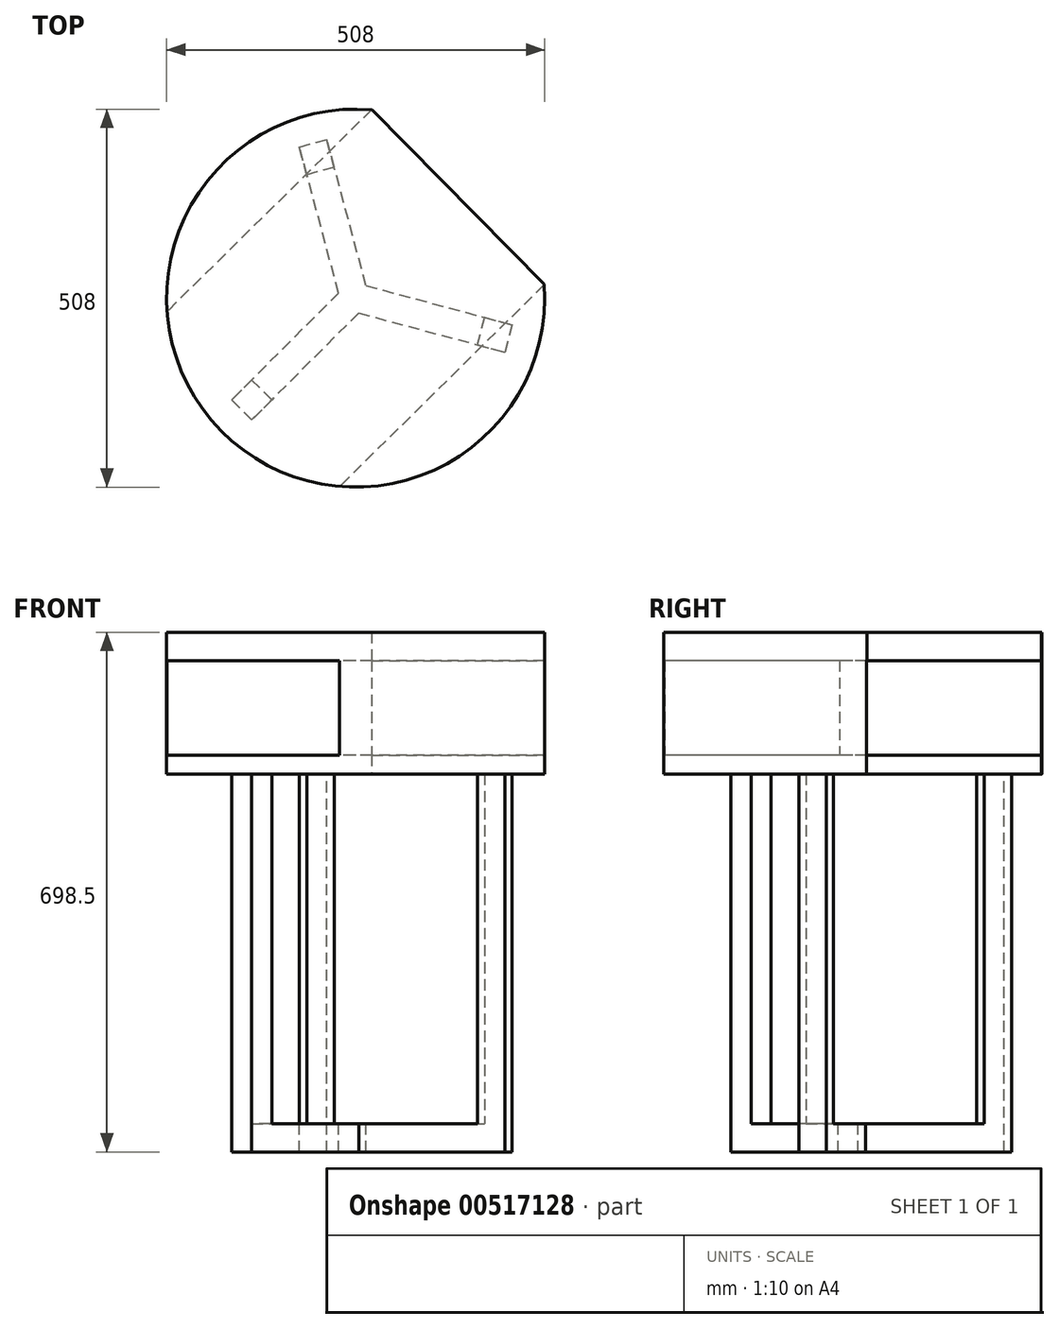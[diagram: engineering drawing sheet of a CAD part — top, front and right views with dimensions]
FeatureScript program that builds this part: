
annotation { "Feature Type Name" : "Feature", "Feature Type Description" : "" }
export const myFeature = defineFeature(function(context is Context, id is Id, definition is map)
    precondition{}
    {
        {
            var Q0;
            Q0=qCreatedBy(makeId("Top.planeOp"),FACE);
            var sketch = newSketch(context, id + "F0", { "sketchPlane" : qUnion([Q0])});
            skLineSegment(sketch, "E0", {"start": v(-200.85, -173.93) * mm, "end": v(-173.93, -200.85) * mm});
            skLineSegment(sketch, "E1", {"start": v(-173.93, -200.85) * mm, "end": v(-164.05, -164.05) * mm});
            skLineSegment(sketch, "E2", {"start": v(-200.85, -173.93) * mm, "end": v(-344.53, -317.6) * mm});
            skLineSegment(sketch, "E3", {"start": v(-173.93, -200.85) * mm, "end": v(-317.63, -344.55) * mm});
            skLineSegment(sketch, "E4", {"start": v(-317.63, -344.55) * mm, "end": v(-344.53, -317.6) * mm});
            skLineSegment(sketch, "E5", {"start": v(-173.93, -200.85) * mm, "end": v(22.33, -253.51) * mm});
            skLineSegment(sketch, "E6", {"start": v(-164.05, -164.05) * mm, "end": v(32.2, -216.71) * mm});
            skLineSegment(sketch, "E7", {"start": v(32.2, -216.71) * mm, "end": v(22.33, -253.51) * mm});
            skLineSegment(sketch, "E8", {"start": v(-200.85, -173.93) * mm, "end": v(-164.05, -164.05) * mm});
            skLineSegment(sketch, "E9", {"start": v(-164.05, -164.05) * mm, "end": v(-216.71, 32.2) * mm});
            skLineSegment(sketch, "E10", {"start": v(-200.85, -173.93) * mm, "end": v(-253.51, 22.33) * mm});
            skLineSegment(sketch, "E11", {"start": v(-253.51, 22.33) * mm, "end": v(-216.71, 32.2) * mm});
            skLineSegment(sketch, "E12", {"start": v(-317.6, -290.67) * mm, "end": v(-290.69, -317.6) * mm});
            skLineSegment(sketch, "E13", {"start": v(-14.47, -243.64) * mm, "end": v(-4.6, -206.84) * mm});
            skLineSegment(sketch, "E14", {"start": v(-243.64, -14.47) * mm, "end": v(-206.84, -4.6) * mm});
            skSolve(sketch);
        }
        {
            var Q0;
            Q0 = qSketchRegion(id + "F0", true);
            extrude(context, id + "F1", {"entities" : qUnion([Q0]), "oppositeDirection" : true, "depth" : 38.1 * mm, "offsetDistance" : 25.4 * mm});
        }
        {
            var Q0;
            {var subQ0=sQuery(id+"F0.wireOp",EDGE,"E4");Q0=makeQuery(id+"F0.imprint","IMPRINT",FACE,{"disambiguationData":[TD([[makeQuery(id+"F0.imprint","IMPRINT",EDGE,{"derivedFrom":subQ0}),-1.0]])]});}
            extrude(context, id + "F2", {"entities" : qUnion([Q0]), "operationType" : NewBodyOperationType.ADD, "depth" : 469.9 * mm, "offsetDistance" : 25.4 * mm});
        }
        {
            var Q0;
            {var subQ0=sQuery(id+"F0.wireOp",EDGE,"E7");Q0=makeQuery(id+"F0.imprint","IMPRINT",FACE,{"disambiguationData":[TD([[makeQuery(id+"F0.imprint","IMPRINT",EDGE,{"derivedFrom":subQ0}),-1.0]])]});}
            extrude(context, id + "F3", {"entities" : qUnion([Q0]), "operationType" : NewBodyOperationType.ADD, "depth" : 469.9 * mm, "offsetDistance" : 25.4 * mm});
        }
        {
            var Q0;
            {var subQ0=sQuery(id+"F0.wireOp",EDGE,"E11");Q0=makeQuery(id+"F0.imprint","IMPRINT",FACE,{"disambiguationData":[TD([[makeQuery(id+"F0.imprint","IMPRINT",EDGE,{"derivedFrom":subQ0}),-1.0]])]});}
            extrude(context, id + "F4", {"entities" : qUnion([Q0]), "operationType" : NewBodyOperationType.ADD, "depth" : 469.9 * mm, "offsetDistance" : 25.4 * mm});
        }
        {
            var Q0;
            Q0=makeQuery(id+"F2.opExtrude","CAP_FACE",FACE,{"disambiguationData":[OSD([sQuery(id+"F0.wireOp",EDGE,"E2"),sQuery(id+"F0.wireOp",EDGE,"E3"),sQuery(id+"F0.wireOp",EDGE,"E4"),sQuery(id+"F0.wireOp",EDGE,"E12")])],"isStart":false});
            var sketch = newSketch(context, id + "F5", { "sketchPlane" : qUnion([Q0])});
            skArc(sketch, "E15", {"start": v(-156.5, 72.26) * mm, "mid": v(-358.81, -359.2) * mm, "end": v(75.38, -162.82) * mm});
            skLineSegment(sketch, "E16", {"start": v(-156.5, 72.26) * mm, "end": v(75.38, -162.82) * mm});
            skPoint(sketch, "E17.end.orphan", {"position": v(-356.35, 0) * mm});
            skSolve(sketch);
        }
        {
            var Q0;
            Q0 = qSketchRegion(id + "F5", true);
            extrude(context, id + "F6", {"entities" : qUnion([Q0]), "operationType" : NewBodyOperationType.ADD, "depth" : 25.4 * mm, "offsetDistance" : 25.4 * mm});
        }
        {
            var Q0;
            Q0=makeQuery(id+"F6.opExtrude","CAP_FACE",FACE,{"disambiguationData":[OSD([sQuery(id+"F5.wireOp",EDGE,"E15")])],"isStart":false});
            var sketch = newSketch(context, id + "F7", { "sketchPlane" : qUnion([Q0])});
            skArc(sketch, "E18", {"start": v(-199.46, -433.92) * mm, "mid": v(0.39, -361.66) * mm, "end": v(75.38, -162.82) * mm});
            skLineSegment(sketch, "E19", {"start": v(75.38, -162.82) * mm, "end": v(137.4, -101.64) * mm});
            skLineSegment(sketch, "E20", {"start": v(75.38, -162.82) * mm, "end": v(-199.46, -433.92) * mm});
            skLineSegment(sketch, "E21", {"start": v(-156.5, 72.26) * mm, "end": v(-431.34, -198.84) * mm});
            skPoint(sketch, "E22.orphan", {"position": v(0.39, -361.66) * mm});
            skPoint(sketch, "E23.end.orphan", {"position": v(-356.35, 0) * mm});
            skArc(sketch, "E24.trimOffspring", {"start": v(-156.5, 72.26) * mm, "mid": v(-356.35, 0) * mm, "end": v(-431.34, -198.84) * mm});
            skLineSegment(sketch, "E25", {"start": v(-199.46, -433.92) * mm, "end": v(-431.34, -198.84) * mm});
            skSolve(sketch);
        }
        {
            var Q0;
            Q0 = qSketchRegion(id + "F7", true);
            extrude(context, id + "F8", {"entities" : qUnion([Q0]), "operationType" : NewBodyOperationType.ADD, "depth" : 127 * mm, "offsetDistance" : 25.4 * mm});
        }
        {
            var Q0;
            Q0=makeQuery(id+"F8.opExtrude","CAP_FACE",FACE,{"disambiguationData":[OSD([sQuery(id+"F7.wireOp",EDGE,"E18"),sQuery(id+"F7.wireOp",EDGE,"E20")])],"isStart":false});
            var sketch = newSketch(context, id + "F9", { "sketchPlane" : qUnion([Q0])});
            skCircle(sketch, "E26", {"center": v(-177.98, -180.83) * mm, "radius": 254 * mm});
            skSolve(sketch);
        }
        {
            var Q0;
            Q0 = qSketchRegion(id + "F9", true);
            extrude(context, id + "F10", {"entities" : qUnion([Q0]), "operationType" : NewBodyOperationType.ADD, "depth" : 38.1 * mm, "offsetDistance" : 25.4 * mm});
        }
        {
            var Q0;
            Q0=makeQuery(id+"F10.opExtrude","CAP_FACE",FACE,{"disambiguationData":[OSD([sQuery(id+"F9.wireOp",EDGE,"E26")])],"isStart":false});
            var sketch = newSketch(context, id + "F11", { "sketchPlane" : qUnion([Q0])});
            skLineSegment(sketch, "E27", {"start": v(-156.15, 72.23) * mm, "end": v(75.33, -162.15) * mm});
            skSolve(sketch);
        }
        {
            var Q0;
            Q0 = qSketchRegion(id + "F11", true);
            var Q1;
            {var subQ0=sQuery(id+"F11.wireOp",EDGE,"E27");Q1=makeQuery(id+"F11.imprint","IMPRINT",FACE,{"disambiguationData":[TD([[makeQuery(id+"F11.imprint","IMPRINT",EDGE,{"derivedFrom":subQ0}),1.0]])]});}
            extrude(context, id + "F12", {"entities" : qUnion([Q0, Q1]), "operationType" : NewBodyOperationType.REMOVE, "oppositeDirection" : true, "depth" : 38.1 * mm, "offsetDistance" : 25.4 * mm});
        }
    });
